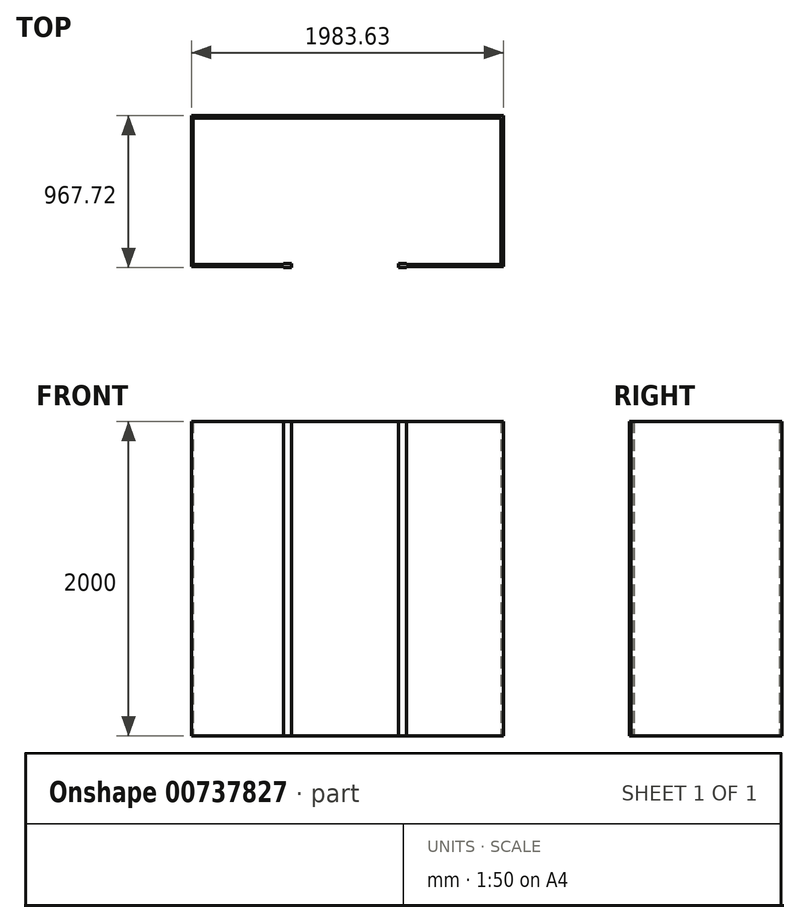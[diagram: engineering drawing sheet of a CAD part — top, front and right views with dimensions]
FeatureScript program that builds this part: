
annotation { "Feature Type Name" : "Feature", "Feature Type Description" : "" }
export const myFeature = defineFeature(function(context is Context, id is Id, definition is map)
    precondition{}
    {
        {
            var Q0;
            Q0=qCreatedBy(makeId("Top.planeOp"),FACE);
            var sketch = newSketch(context, id + "F0", { "sketchPlane" : qUnion([Q0])});
            skLineSegment(sketch, "E0", {"start": v(-398.07, -302.66) * mm, "end": v(-398.07, 627.34) * mm});
            skLineSegment(sketch, "E1", {"start": v(-398.07, 627.34) * mm, "end": v(1556.93, 627.34) * mm});
            skLineSegment(sketch, "E2", {"start": v(1556.93, 627.34) * mm, "end": v(1556.93, -302.66) * mm});
            skLineSegment(sketch, "E3", {"start": v(1556.93, -302.66) * mm, "end": v(956.93, -302.66) * mm});
            skLineSegment(sketch, "E4", {"start": v(176.93, -302.66) * mm, "end": v(-398.07, -302.66) * mm});
            skLineSegment(sketch, "E5", {"start": v(176.93, -302.66) * mm, "end": v(176.93, -294.06) * mm});
            skLineSegment(sketch, "E6", {"start": v(176.93, -294.06) * mm, "end": v(226.93, -294.06) * mm});
            skLineSegment(sketch, "E7", {"start": v(226.93, -294.06) * mm, "end": v(226.93, -322.17) * mm});
            skLineSegment(sketch, "E8", {"start": v(226.93, -322.17) * mm, "end": v(176.93, -322.17) * mm});
            skLineSegment(sketch, "E9", {"start": v(176.93, -322.17) * mm, "end": v(176.93, -313.57) * mm});
            skLineSegment(sketch, "E10", {"start": v(176.93, -313.57) * mm, "end": v(-408.55, -313.57) * mm});
            skLineSegment(sketch, "E11", {"start": v(-408.55, -313.57) * mm, "end": v(-408.55, 645.55) * mm});
            skLineSegment(sketch, "E12", {"start": v(-408.55, 645.55) * mm, "end": v(1575.08, 645.55) * mm});
            skLineSegment(sketch, "E13", {"start": v(1575.08, 645.55) * mm, "end": v(1575.08, -313.57) * mm});
            skLineSegment(sketch, "E14", {"start": v(1575.08, -313.57) * mm, "end": v(956.93, -313.57) * mm});
            skLineSegment(sketch, "E15", {"start": v(956.93, -313.57) * mm, "end": v(956.93, -322.17) * mm});
            skLineSegment(sketch, "E16", {"start": v(956.93, -322.17) * mm, "end": v(906.93, -322.17) * mm});
            skLineSegment(sketch, "E17", {"start": v(906.93, -322.17) * mm, "end": v(906.93, -294.06) * mm});
            skLineSegment(sketch, "E18", {"start": v(906.93, -294.06) * mm, "end": v(956.93, -294.06) * mm});
            skLineSegment(sketch, "E19", {"start": v(956.93, -294.06) * mm, "end": v(956.93, -302.66) * mm});
            skSolve(sketch);
        }
        {
            var Q0;
            Q0 = qSketchRegion(id + "F0", true);
            extrude(context, id + "F1", {"entities" : qUnion([Q0]), "depth" : 2000 * mm, "offsetDistance" : 25 * mm});
        }
    });
